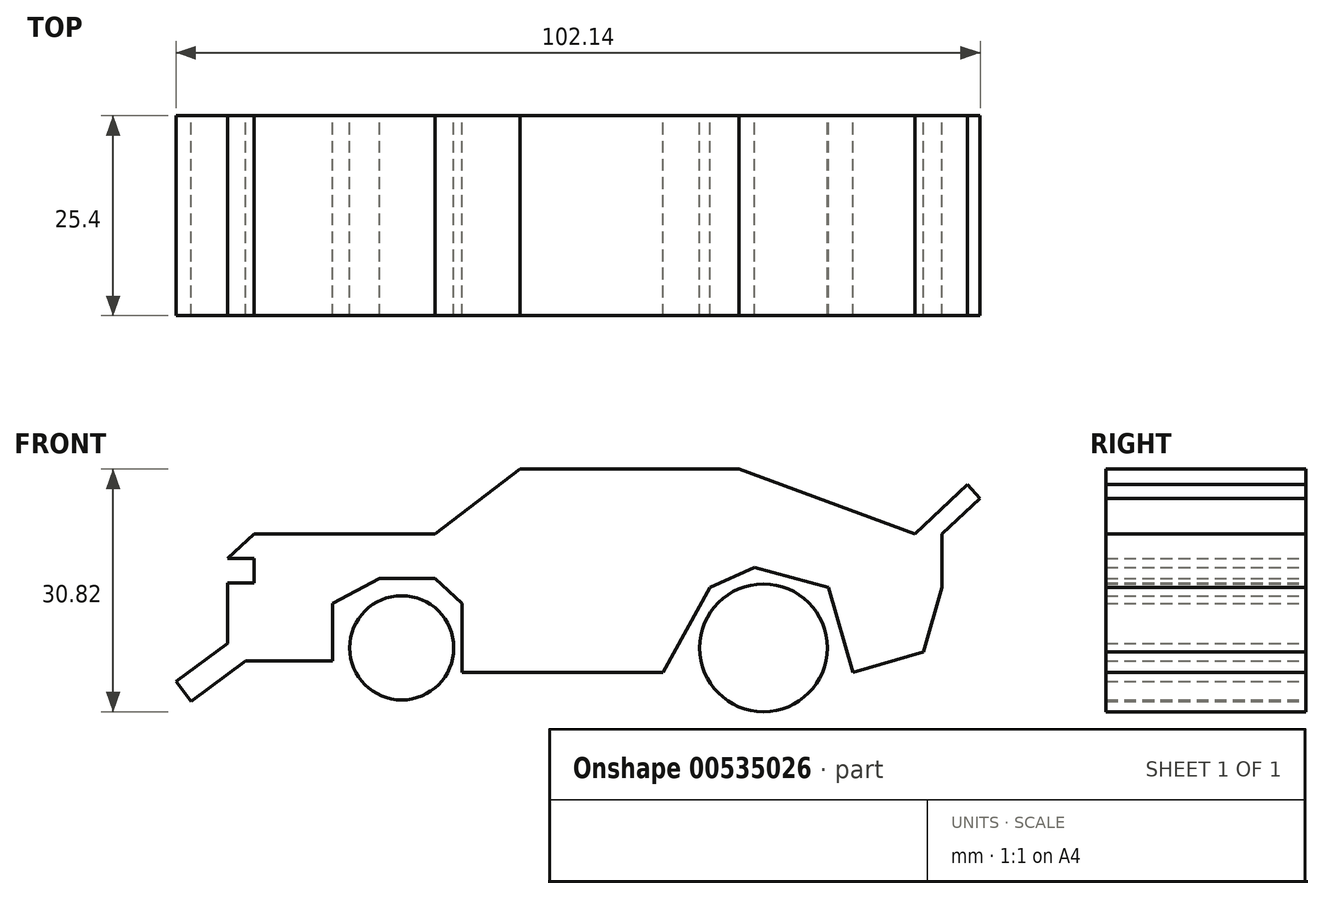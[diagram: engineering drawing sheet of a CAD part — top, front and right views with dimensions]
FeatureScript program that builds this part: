
annotation { "Feature Type Name" : "Feature", "Feature Type Description" : "" }
export const myFeature = defineFeature(function(context is Context, id is Id, definition is map)
    precondition{}
    {
        {
            var Q0;
            Q0=qCreatedBy(makeId("Front.planeOp"),FACE);
            var sketch = newSketch(context, id + "F0", { "sketchPlane" : qUnion([Q0])});
            skCircle(sketch, "E0", {"center": v(-18.87, 6.8) * mm, "radius": 6.62 * mm});
            skCircle(sketch, "E1", {"center": v(27.1, 6.8) * mm, "radius": 8.11 * mm});
            skSolve(sketch);
        }
        {
            var Q0;
            Q0=makeQuery(id+"F0.imprint","IMPRINT",FACE,{"disambiguationData":[TD([[makeQuery(id+"F0.imprint","IMPRINT",EDGE,{"derivedFrom":sQuery(id+"F0.wireOp",EDGE,"E1")}),1.0]])]});
            var Q1;
            Q1=makeQuery(id+"F0.imprint","IMPRINT",FACE,{"disambiguationData":[TD([[makeQuery(id+"F0.imprint","IMPRINT",EDGE,{"derivedFrom":sQuery(id+"F0.wireOp",EDGE,"E0")}),1.0]])]});
            extrude(context, id + "F1", {"entities" : qUnion([Q0, Q1]), "depth" : 25.4 * mm, "offsetDistance" : 25.4 * mm});
        }
        {
            var Q0;
            Q0=qCreatedBy(makeId("Front.planeOp"),FACE);
            var sketch = newSketch(context, id + "F2", { "sketchPlane" : qUnion([Q0])});
            skLineSegment(sketch, "E2", {"start": v(-11.2, 3.69) * mm, "end": v(14.33, 3.69) * mm});
            skLineSegment(sketch, "E3", {"start": v(14.33, 3.69) * mm, "end": v(20.29, 14.47) * mm});
            skLineSegment(sketch, "E4", {"start": v(20.29, 14.47) * mm, "end": v(25.96, 17.02) * mm});
            skLineSegment(sketch, "E5", {"start": v(25.96, 17.02) * mm, "end": v(35.32, 14.47) * mm});
            skLineSegment(sketch, "E6", {"start": v(35.32, 14.47) * mm, "end": v(38.44, 3.69) * mm});
            skLineSegment(sketch, "E7", {"start": v(38.44, 3.69) * mm, "end": v(47.43, 6.29) * mm});
            skLineSegment(sketch, "E8", {"start": v(47.43, 6.29) * mm, "end": v(49.8, 14.47) * mm});
            skLineSegment(sketch, "E9", {"start": v(49.8, 14.47) * mm, "end": v(49.8, 21.28) * mm});
            skLineSegment(sketch, "E10", {"start": v(49.8, 21.28) * mm, "end": v(54.62, 25.82) * mm});
            skLineSegment(sketch, "E11", {"start": v(54.62, 25.82) * mm, "end": v(53, 27.54) * mm});
            skLineSegment(sketch, "E12", {"start": v(53, 27.54) * mm, "end": v(46.34, 21.28) * mm});
            skLineSegment(sketch, "E13", {"start": v(46.34, 21.28) * mm, "end": v(23.97, 29.5) * mm});
            skLineSegment(sketch, "E14", {"start": v(23.97, 29.5) * mm, "end": v(-3.83, 29.5) * mm});
            skLineSegment(sketch, "E15", {"start": v(-3.83, 29.5) * mm, "end": v(-14.61, 21.28) * mm});
            skLineSegment(sketch, "E16", {"start": v(-14.61, 21.28) * mm, "end": v(-37.6, 21.28) * mm});
            skLineSegment(sketch, "E17", {"start": v(-37.6, 21.28) * mm, "end": v(-41, 18.16) * mm});
            skLineSegment(sketch, "E18", {"start": v(-41, 18.16) * mm, "end": v(-37.6, 18.16) * mm});
            skLineSegment(sketch, "E19", {"start": v(-37.6, 18.16) * mm, "end": v(-37.6, 15.04) * mm});
            skLineSegment(sketch, "E20", {"start": v(-37.6, 15.04) * mm, "end": v(-41, 15.04) * mm});
            skLineSegment(sketch, "E21", {"start": v(-41, 15.04) * mm, "end": v(-41, 7.38) * mm});
            skLineSegment(sketch, "E22", {"start": v(-41, 7.38) * mm, "end": v(-47.52, 2.55) * mm});
            skLineSegment(sketch, "E23", {"start": v(-47.52, 2.55) * mm, "end": v(-45.64, 0) * mm});
            skLineSegment(sketch, "E24", {"start": v(-45.64, 0) * mm, "end": v(-38.68, 5.14) * mm});
            skLineSegment(sketch, "E25", {"start": v(-38.68, 5.14) * mm, "end": v(-27.66, 5.14) * mm});
            skLineSegment(sketch, "E26", {"start": v(-27.66, 5.14) * mm, "end": v(-27.66, 12.48) * mm});
            skLineSegment(sketch, "E27", {"start": v(-27.66, 12.48) * mm, "end": v(-21.7, 15.6) * mm});
            skLineSegment(sketch, "E28", {"start": v(-21.7, 15.6) * mm, "end": v(-14.61, 15.6) * mm});
            skLineSegment(sketch, "E29", {"start": v(-14.61, 15.6) * mm, "end": v(-11.2, 12.48) * mm});
            skLineSegment(sketch, "E30", {"start": v(-11.2, 12.48) * mm, "end": v(-11.2, 3.69) * mm});
            skSolve(sketch);
        }
        {
            var Q0;
            Q0=makeQuery(id+"F2.imprint","IMPRINT",FACE,{"disambiguationData":[TD([[makeQuery(id+"F2.imprint","IMPRINT",EDGE,{"derivedFrom":sQuery(id+"F2.wireOp",EDGE,"E2")}),1.0]])]});
            extrude(context, id + "F3", {"entities" : qUnion([Q0]), "depth" : 25.4 * mm, "offsetDistance" : 25.4 * mm});
        }
    });
